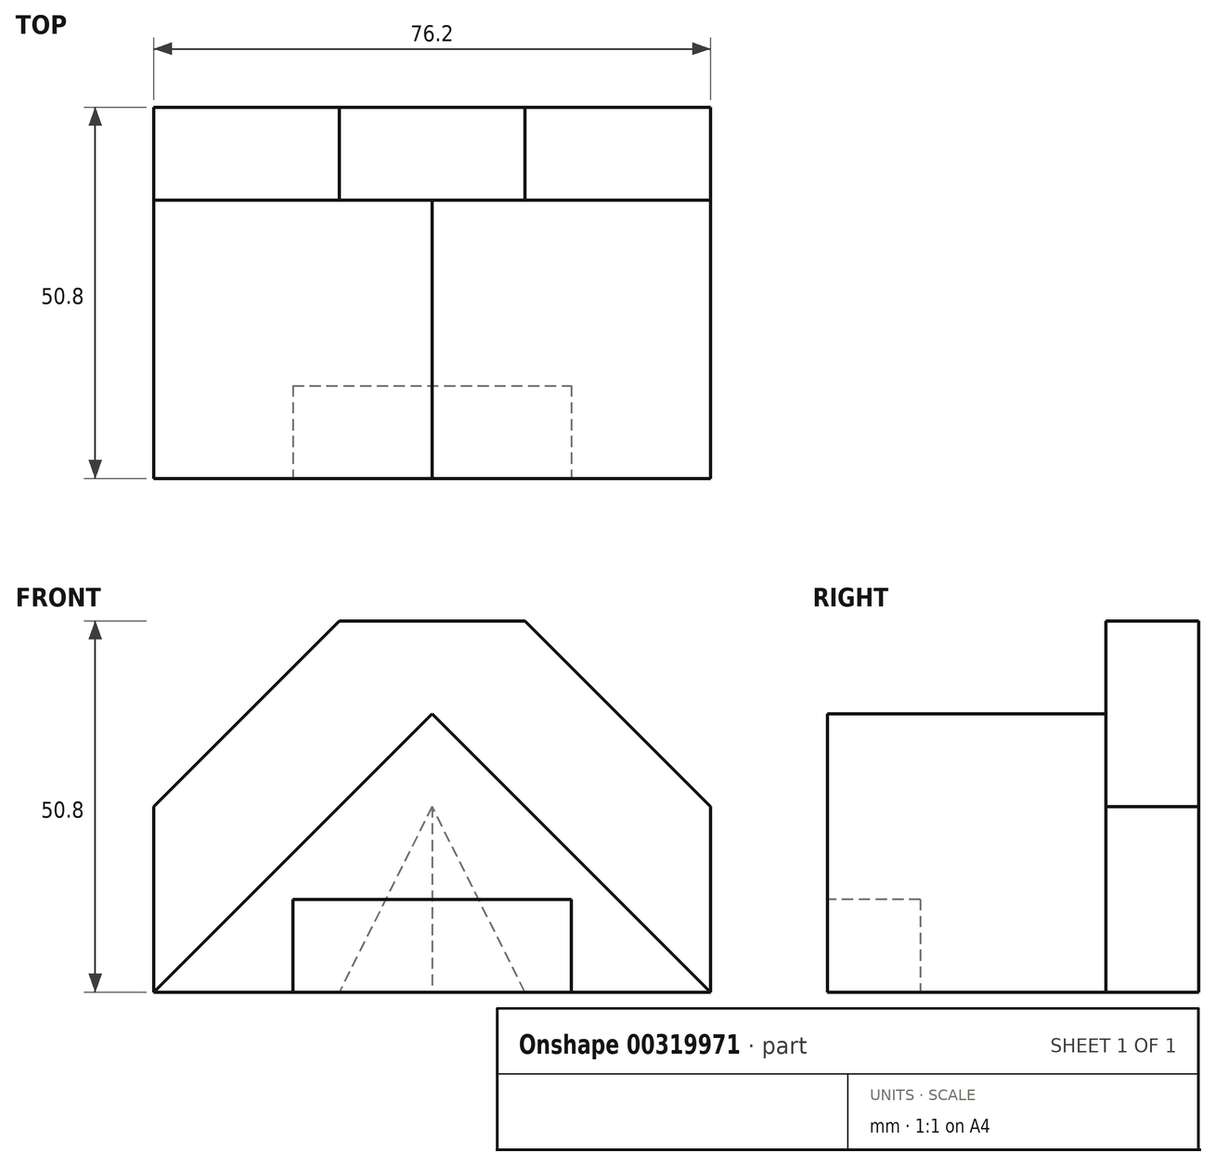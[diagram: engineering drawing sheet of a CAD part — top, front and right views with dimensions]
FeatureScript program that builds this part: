
annotation { "Feature Type Name" : "Feature", "Feature Type Description" : "" }
export const myFeature = defineFeature(function(context is Context, id is Id, definition is map)
    precondition{}
    {
        {
            var Q0;
            Q0=qCreatedBy(makeId("Front.planeOp"),FACE);
            var sketch = newSketch(context, id + "F0", { "sketchPlane" : qUnion([Q0])});
            skLineSegment(sketch, "E0", {"start": v(-38.1, 0) * mm, "end": v(-38.1, 25.4) * mm});
            skLineSegment(sketch, "E1", {"start": v(-38.1, 25.4) * mm, "end": v(-12.7, 50.8) * mm});
            skLineSegment(sketch, "E2", {"start": v(-12.7, 50.8) * mm, "end": v(12.7, 50.8) * mm});
            skLineSegment(sketch, "E3", {"start": v(12.7, 50.8) * mm, "end": v(38.1, 25.4) * mm});
            skLineSegment(sketch, "E4", {"start": v(38.1, 25.4) * mm, "end": v(38.1, 0) * mm});
            skLineSegment(sketch, "E5", {"start": v(38.1, 0) * mm, "end": v(-38.1, 0) * mm});
            skLineSegment(sketch, "E6", {"start": v(0, 0) * mm, "end": v(0, 78.5) * mm, "construction": true});
            skLineSegment(sketch, "E7", {"start": v(-38.1, 0) * mm, "end": v(38.1, 0) * mm});
            skSolve(sketch);
        }
        {
            var Q0;
            Q0=makeQuery(id+"F0.imprint","IMPRINT",FACE,{"disambiguationData":[TD([[makeQuery(id+"F0.imprint","IMPRINT",EDGE,{"derivedFrom":sQuery(id+"F0.wireOp",EDGE,"E0")}),-1.0]])]});
            var Q1;
            Q1=makeQuery(id+"F0.imprint","IMPRINT",FACE,{"disambiguationData":[TD([[makeQuery(id+"F0.imprint","IMPRINT",EDGE,{"derivedFrom":sQuery(id+"F0.wireOp",EDGE,"hnHXZbLU-3TWf-XzZc-uTzp-QzwT8sh10Lem")}),-1.0]])]});
            extrude(context, id + "F1", {"entities" : qUnion([Q0, Q1]), "depth" : 12.7 * mm});
        }
        {
            var Q0;
            Q0=makeQuery(id+"F1.opExtrude","CAP_FACE",FACE,{"disambiguationData":[OSD([sQuery(id+"F0.wireOp",EDGE,"E0"),sQuery(id+"F0.wireOp",EDGE,"E1"),sQuery(id+"F0.wireOp",EDGE,"E2"),sQuery(id+"F0.wireOp",EDGE,"E3"),sQuery(id+"F0.wireOp",EDGE,"E4"),sQuery(id+"F0.wireOp",EDGE,"E7")])],"isStart":false});
            var sketch = newSketch(context, id + "F2", { "sketchPlane" : qUnion([Q0])});
            skLineSegment(sketch, "E8", {"start": v(-38.1, 0) * mm, "end": v(0, 38.1) * mm});
            skLineSegment(sketch, "E9", {"start": v(0, 38.1) * mm, "end": v(38.1, 0) * mm});
            skLineSegment(sketch, "E10", {"start": v(38.1, 0) * mm, "end": v(-38.1, 0) * mm});
            skSolve(sketch);
        }
        {
            var Q0;
            Q0=makeQuery(id+"F2.imprint","IMPRINT",FACE,{"disambiguationData":[TD([[makeQuery(id+"F2.imprint","IMPRINT",EDGE,{"derivedFrom":sQuery(id+"F2.wireOp",EDGE,"E8")}),-1.0]])]});
            extrude(context, id + "F3", {"entities" : qUnion([Q0]), "operationType" : NewBodyOperationType.ADD, "depth" : 38.1 * mm});
        }
        {
            var Q0;
            Q0=makeQuery(id+"F3.opExtrude","CAP_EDGE",EDGE,{"disambiguationData":[OSD([sQuery(id+"F2.wireOp",EDGE,"E10")])],"isStart":false});
            cPlane(context, id + "F4", {"entities" : qUnion([Q0]), "cplaneType" : CPlaneType.LINE_ANGLE, "offset" : 25.4 * mm, "angle" : 45 * degree, "oppositeDirection" : true, "width" : 152.4 * mm, "height" : 152.4 * mm});
        }
        {
            var Q0;
            Q0=qCreatedBy(id+"F4.planeOp",FACE);
            var sketch = newSketch(context, id + "F5", { "sketchPlane" : qUnion([Q0])});
            skLineSegment(sketch, "E11.0", {"start": v(38.1, -35.92) * mm, "end": v(-38.1, -35.92) * mm});
            skLineSegment(sketch, "E12.0", {"start": v(38.1, -8.98) * mm, "end": v(0, 17.96) * mm});
            skLineSegment(sketch, "E13.0", {"start": v(0, 17.96) * mm, "end": v(-38.1, -8.98) * mm});
            skLineSegment(sketch, "E14", {"start": v(38.1, -35.92) * mm, "end": v(0, 17.96) * mm});
            skLineSegment(sketch, "E15", {"start": v(0, 17.96) * mm, "end": v(-38.1, -35.92) * mm});
            skSolve(sketch);
        }
        {
            var Q0;
            Q0 = qSketchRegion(id + "F5", true);
            extrude(context, id + "F6", {"entities" : qUnion([Q0]), "operationType" : NewBodyOperationType.REMOVE, "endBound" : BoundingType.THROUGH_ALL, "oppositeDirection" : true, "depth" : 25.4 * mm});
        }
        {
            var Q0;
            Q0=qCreatedBy(makeId("Front.planeOp"),FACE);
            cPlane(context, id + "F7", {"entities" : qUnion([Q0]), "cplaneType" : CPlaneType.OFFSET, "offset" : 50.8 * mm, "width" : 152.4 * mm, "height" : 152.4 * mm});
        }
        {
            var Q0;
            Q0=qCreatedBy(id+"F7.planeOp",FACE);
            var sketch = newSketch(context, id + "F8", { "sketchPlane" : qUnion([Q0])});
            skLineSegment(sketch, "E16.bottom", {"start": v(-19.05, 12.7) * mm, "end": v(19.05, 12.7) * mm});
            skLineSegment(sketch, "E16.top", {"start": v(-19.05, 0) * mm, "end": v(19.05, 0) * mm});
            skLineSegment(sketch, "E16.left", {"start": v(-19.05, 12.7) * mm, "end": v(-19.05, 0) * mm});
            skLineSegment(sketch, "E16.right", {"start": v(19.05, 12.7) * mm, "end": v(19.05, 0) * mm});
            skSolve(sketch);
        }
        {
            var Q0;
            Q0=makeQuery(id+"F8.imprint","IMPRINT",FACE,{"disambiguationData":[TD([[makeQuery(id+"F8.imprint","IMPRINT",EDGE,{"derivedFrom":sQuery(id+"F8.wireOp",EDGE,"E16.bottom")}),-1.0]])]});
            extrude(context, id + "F9", {"entities" : qUnion([Q0]), "operationType" : NewBodyOperationType.REMOVE, "oppositeDirection" : true, "depth" : 12.7 * mm});
        }
    });
